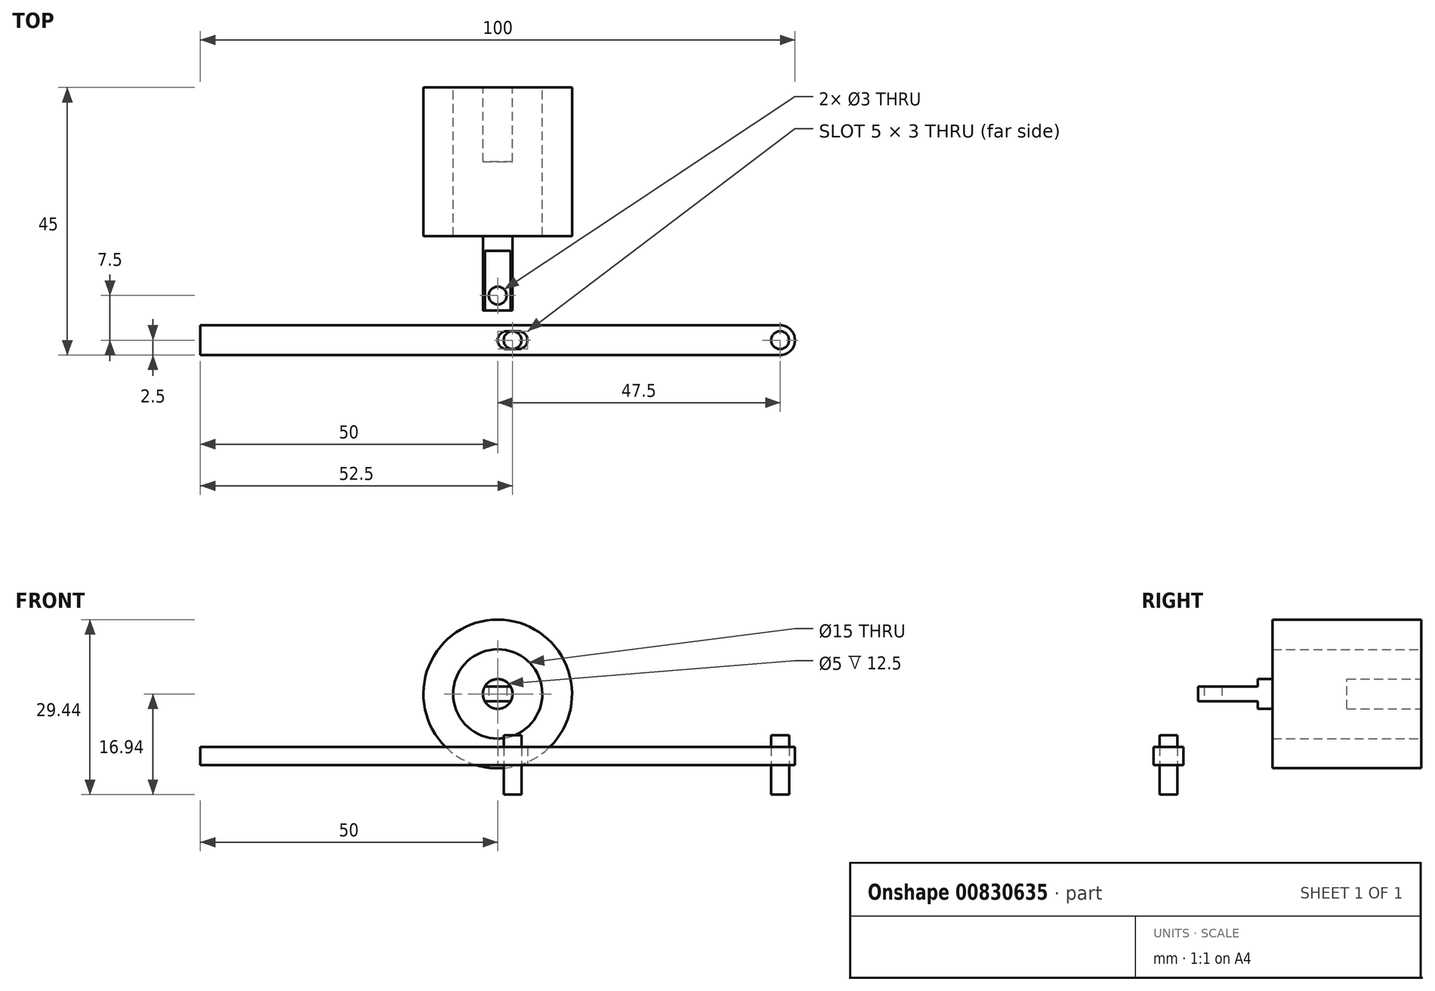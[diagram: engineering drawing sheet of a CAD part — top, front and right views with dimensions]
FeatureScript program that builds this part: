
annotation { "Feature Type Name" : "Feature", "Feature Type Description" : "" }
export const myFeature = defineFeature(function(context is Context, id is Id, definition is map)
    precondition{}
    {
        {
            var Q0;
            Q0=qCreatedBy(makeId("Top.planeOp"),FACE);
            var sketch = newSketch(context, id + "F0", { "sketchPlane" : qUnion([Q0])});
            skLineSegment(sketch, "E0.bottom", {"start": v(50, 2.5) * mm, "end": v(-50, 2.5) * mm});
            skLineSegment(sketch, "E0.top", {"start": v(50, -2.5) * mm, "end": v(-50, -2.5) * mm});
            skLineSegment(sketch, "E0.left", {"start": v(50, 2.5) * mm, "end": v(50, -2.5) * mm});
            skLineSegment(sketch, "E0.right", {"start": v(-50, 2.5) * mm, "end": v(-50, -2.5) * mm});
            skPoint(sketch, "E0.middle", {"position": v(0, 0) * mm});
            skCircle(sketch, "E1", {"center": v(47.5, 0) * mm, "radius": 1.5 * mm});
            skPoint(sketch, "E2.visualSharp", {"position": v(50, 2.5) * mm});
            skPoint(sketch, "E3.visualSharp", {"position": v(50, -2.5) * mm});
            skCircle(sketch, "E4", {"center": v(2.5, 0) * mm, "radius": 1.5 * mm});
            skLineSegment(sketch, "E5.bottom", {"start": v(5, -1.5) * mm, "end": v(0, -1.5) * mm});
            skLineSegment(sketch, "E5.top", {"start": v(5, 1.5) * mm, "end": v(0, 1.5) * mm});
            skLineSegment(sketch, "E5.left", {"start": v(5, -1.5) * mm, "end": v(5, 1.5) * mm});
            skLineSegment(sketch, "E5.right", {"start": v(0, -1.5) * mm, "end": v(0, 1.5) * mm});
            skCircle(sketch, "E6", {"center": v(1.5, 0) * mm, "radius": 1.5 * mm});
            skCircle(sketch, "E7", {"center": v(3.5, 0) * mm, "radius": 1.5 * mm});
            skCircle(sketch, "E8", {"center": v(47.5, 0) * mm, "radius": 2.5 * mm});
            skSolve(sketch);
        }
        {
            var Q0;
            {var subQ0=sQuery(id+"F0.wireOp",EDGE,"E5.right");var subQ1=sQuery(id+"F0.wireOp",EDGE,"E5.top");var subQ2=makeQuery(id+"F0.imprint","INTERSECT",VERTEX,{"derivedFrom":[subQ1,subQ0]});Q0=makeQuery(id+"F0.imprint","IMPRINT",FACE,{"disambiguationData":[TD([[makeQuery(id+"F0.imprint","IMPRINT",EDGE,{"disambiguationData":[TD([[subQ2,1.0]])],"derivedFrom":subQ1}),1.0]])]});}
            var Q1;
            {var subQ0=sQuery(id+"F0.wireOp",EDGE,"E5.right");var subQ1=sQuery(id+"F0.wireOp",EDGE,"E5.bottom");var subQ2=makeQuery(id+"F0.imprint","INTERSECT",VERTEX,{"derivedFrom":[subQ1,subQ0]});Q1=makeQuery(id+"F0.imprint","IMPRINT",FACE,{"disambiguationData":[TD([[makeQuery(id+"F0.imprint","IMPRINT",EDGE,{"disambiguationData":[TD([[subQ2,1.0]])],"derivedFrom":subQ1}),-1.0]])]});}
            var Q2;
            {var subQ0=sQuery(id+"F0.wireOp",EDGE,"E5.left");var subQ1=sQuery(id+"F0.wireOp",EDGE,"E5.bottom");var subQ2=makeQuery(id+"F0.imprint","INTERSECT",VERTEX,{"derivedFrom":[subQ1,subQ0]});Q2=makeQuery(id+"F0.imprint","IMPRINT",FACE,{"disambiguationData":[TD([[makeQuery(id+"F0.imprint","IMPRINT",EDGE,{"disambiguationData":[TD([[subQ2,-1.0]])],"derivedFrom":subQ1}),-1.0]])]});}
            var Q3;
            {var subQ0=sQuery(id+"F0.wireOp",EDGE,"E5.left");var subQ1=sQuery(id+"F0.wireOp",EDGE,"E5.top");var subQ2=makeQuery(id+"F0.imprint","INTERSECT",VERTEX,{"derivedFrom":[subQ1,subQ0]});Q3=makeQuery(id+"F0.imprint","IMPRINT",FACE,{"disambiguationData":[TD([[makeQuery(id+"F0.imprint","IMPRINT",EDGE,{"disambiguationData":[TD([[subQ2,-1.0]])],"derivedFrom":subQ1}),1.0]])]});}
            var Q4;
            {var subQ13=sQuery(id+"F0.wireOp",EDGE,"E0.right");Q4=makeQuery(id+"F0.imprint","IMPRINT",FACE,{"disambiguationData":[TD([[makeQuery(id+"F0.imprint","IMPRINT",EDGE,{"derivedFrom":subQ13}),1.0]])]});}
            var Q5;
            Q5=makeQuery(id+"F0.imprint","IMPRINT",FACE,{"disambiguationData":[TD([[makeQuery(id+"F0.imprint","IMPRINT",EDGE,{"derivedFrom":sQuery(id+"F0.wireOp",EDGE,"E1")}),-1.0]])]});
            extrude(context, id + "F1", {"entities" : qUnion([Q0, Q1, Q2, Q3, Q4, Q5]), "depth" : 3 * mm, "offsetDistance" : 25 * mm});
        }
        {
            var Q0;
            Q0=makeQuery(id+"F0.imprint","IMPRINT",FACE,{"disambiguationData":[TD([[makeQuery(id+"F0.imprint","IMPRINT",EDGE,{"derivedFrom":sQuery(id+"F0.wireOp",EDGE,"E4")}),1.0]])]});
            var Q1;
            Q1=makeQuery(id+"F0.imprint","IMPRINT",FACE,{"disambiguationData":[TD([[makeQuery(id+"F0.imprint","IMPRINT",EDGE,{"derivedFrom":sQuery(id+"F0.wireOp",EDGE,"E1")}),1.0]])]});
            var Q2;
            {var subQ0=sQuery(id+"F0.wireOp",EDGE,"E6");var subQ1=sQuery(id+"F0.wireOp",EDGE,"E4");var subQ2=makeQuery(id+"F0.imprint","INTERSECT",VERTEX,{"disambiguationData":[OD(0.0)],"derivedFrom":[subQ1,subQ0]});Q2=makeQuery(id+"F0.imprint","IMPRINT",FACE,{"disambiguationData":[TD([[makeQuery(id+"F0.imprint","IMPRINT",EDGE,{"disambiguationData":[TD([[subQ2,-1.0]])],"derivedFrom":subQ1}),1.0]])]});}
            var Q3;
            {var subQ0=sQuery(id+"F0.wireOp",EDGE,"E7");var subQ1=sQuery(id+"F0.wireOp",EDGE,"E4");var subQ2=makeQuery(id+"F0.imprint","INTERSECT",VERTEX,{"disambiguationData":[OD(0.0)],"derivedFrom":[subQ1,subQ0]});Q3=makeQuery(id+"F0.imprint","IMPRINT",FACE,{"disambiguationData":[TD([[makeQuery(id+"F0.imprint","IMPRINT",EDGE,{"disambiguationData":[TD([[subQ2,1.0]])],"derivedFrom":subQ1}),1.0]])]});}
            var Q4;
            {var subQ0=sQuery(id+"F0.wireOp",EDGE,"E7");var subQ1=sQuery(id+"F0.wireOp",EDGE,"E6");var subQ2=makeQuery(id+"F0.imprint","INTERSECT",VERTEX,{"disambiguationData":[OD(0.0)],"derivedFrom":[subQ1,subQ0]});Q4=makeQuery(id+"F0.imprint","IMPRINT",FACE,{"disambiguationData":[TD([[makeQuery(id+"F0.imprint","IMPRINT",EDGE,{"disambiguationData":[TD([[subQ2,1.0]])],"derivedFrom":subQ1}),1.0]])]});}
            extrude(context, id + "F2", {"entities" : qUnion([Q0, Q1, Q2, Q3, Q4]), "endBound" : BoundingType.SYMMETRIC, "depth" : 10 * mm, "offsetDistance" : 25 * mm});
        }
        {
            var Q0;
            Q0=qCreatedBy(makeId("Front.planeOp"),FACE);
            cPlane(context, id + "F3", {"entities" : qUnion([Q0]), "cplaneType" : CPlaneType.OFFSET, "offset" : 30 * mm, "oppositeDirection" : true, "width" : 150 * mm, "height" : 150 * mm});
        }
        {
            var Q0;
            Q0=qCreatedBy(id+"F3.planeOp",FACE);
            var sketch = newSketch(context, id + "F4", { "sketchPlane" : qUnion([Q0])});
            skCircle(sketch, "E9", {"center": v(0, 11.94) * mm, "radius": 12.5 * mm});
            skCircle(sketch, "E10", {"center": v(0, 11.94) * mm, "radius": 7.5 * mm});
            skCircle(sketch, "E11", {"center": v(0, 11.94) * mm, "radius": 2.5 * mm});
            skSolve(sketch);
        }
        {
            var Q0;
            Q0=makeQuery(id+"F4.imprint","IMPRINT",FACE,{"disambiguationData":[TD([[makeQuery(id+"F4.imprint","IMPRINT",EDGE,{"derivedFrom":sQuery(id+"F4.wireOp",EDGE,"E9")}),1.0]])]});
            extrude(context, id + "F5", {"entities" : qUnion([Q0]), "endBound" : BoundingType.SYMMETRIC, "depth" : 25 * mm, "offsetDistance" : 25 * mm});
        }
        {
            var Q0;
            Q0=makeQuery(id+"F4.imprint","IMPRINT",FACE,{"disambiguationData":[TD([[makeQuery(id+"F4.imprint","IMPRINT",EDGE,{"derivedFrom":sQuery(id+"F4.wireOp",EDGE,"E10")}),1.0]])]});
            extrude(context, id + "F6", {"entities" : qUnion([Q0]), "endBound" : BoundingType.SYMMETRIC, "depth" : 25 * mm, "offsetDistance" : 25 * mm});
        }
        {
            var Q0;
            Q0=makeQuery(id+"F4.imprint","IMPRINT",FACE,{"disambiguationData":[TD([[makeQuery(id+"F4.imprint","IMPRINT",EDGE,{"derivedFrom":sQuery(id+"F4.wireOp",EDGE,"E11")}),1.0]])]});
            extrude(context, id + "F7", {"entities" : qUnion([Q0]), "operationType" : NewBodyOperationType.ADD, "depth" : 25 * mm, "offsetDistance" : 25 * mm});
        }
        {
            var Q0;
            Q0=makeQuery(id+"F7.opExtrude","CAP_FACE",FACE,{"disambiguationData":[OSD([sQuery(id+"F4.wireOp",EDGE,"E11")])],"isStart":false});
            var sketch = newSketch(context, id + "F8", { "sketchPlane" : qUnion([Q0])});
            skLineSegment(sketch, "E12.bottom", {"start": v(3.5, 8.44) * mm, "end": v(-3.5, 8.44) * mm});
            skLineSegment(sketch, "E12.top", {"start": v(3.5, 15.44) * mm, "end": v(-3.5, 15.44) * mm});
            skLineSegment(sketch, "E12.left", {"start": v(3.5, 8.44) * mm, "end": v(3.5, 15.44) * mm});
            skLineSegment(sketch, "E12.right", {"start": v(-3.5, 8.44) * mm, "end": v(-3.5, 15.44) * mm});
            skPoint(sketch, "E12.middle", {"position": v(0, 11.94) * mm});
            skLineSegment(sketch, "E13.bottom", {"start": v(3.5, 13.19) * mm, "end": v(-3.5, 13.19) * mm});
            skLineSegment(sketch, "E13.top", {"start": v(3.5, 10.69) * mm, "end": v(-3.5, 10.69) * mm});
            skLineSegment(sketch, "E13.left", {"start": v(3.5, 13.19) * mm, "end": v(3.5, 10.69) * mm});
            skLineSegment(sketch, "E13.right", {"start": v(-3.5, 13.19) * mm, "end": v(-3.5, 10.69) * mm});
            skSolve(sketch);
        }
        {
            var Q0;
            {var subQ0=sQuery(id+"F8.wireOp",EDGE,"Uzw0eZBX-GlzA-F4h8-tydv-80rBA1psysMD");var subQ1=makeQuery(id+"F7.opExtrude","CAP_EDGE",EDGE,{"disambiguationData":[OSD([sQuery(id+"F4.wireOp",EDGE,"E11")])],"isStart":false});var subQ2=makeQuery(id+"F8.imprint","INTERSECT",VERTEX,{"disambiguationData":[OD(0.0)],"derivedFrom":[subQ1,subQ0]});Q0=makeQuery(id+"F8.imprint","IMPRINT",FACE,{"disambiguationData":[TD([[makeQuery(id+"F8.imprint","IMPRINT",EDGE,{"disambiguationData":[TD([[subQ2,-1.0]])],"derivedFrom":subQ0}),-1.0]])]});}
            var Q1;
            {var subQ0=sQuery(id+"F8.wireOp",EDGE,"E13.top");var subQ1=makeQuery(id+"F7.opExtrude","CAP_EDGE",EDGE,{"disambiguationData":[OSD([sQuery(id+"F4.wireOp",EDGE,"E11")])],"isStart":false});var subQ2=makeQuery(id+"F8.imprint","INTERSECT",VERTEX,{"disambiguationData":[OD(0.0)],"derivedFrom":[subQ1,subQ0]});Q1=makeQuery(id+"F8.imprint","IMPRINT",FACE,{"disambiguationData":[TD([[makeQuery(id+"F8.imprint","IMPRINT",EDGE,{"disambiguationData":[TD([[subQ2,-1.0]])],"derivedFrom":subQ0}),1.0]])]});}
            var Q2;
            {var subQ0=sQuery(id+"F8.wireOp",EDGE,"E13.bottom");var subQ1=makeQuery(id+"F7.opExtrude","CAP_EDGE",EDGE,{"disambiguationData":[OSD([sQuery(id+"F4.wireOp",EDGE,"E11")])],"isStart":false});var subQ2=makeQuery(id+"F8.imprint","INTERSECT",VERTEX,{"disambiguationData":[OD(0.0)],"derivedFrom":[subQ1,subQ0]});Q2=makeQuery(id+"F8.imprint","IMPRINT",FACE,{"disambiguationData":[TD([[makeQuery(id+"F8.imprint","IMPRINT",EDGE,{"disambiguationData":[TD([[subQ2,-1.0]])],"derivedFrom":subQ0}),-1.0]])]});}
            extrude(context, id + "F9", {"entities" : qUnion([Q0, Q1, Q2]), "operationType" : NewBodyOperationType.REMOVE, "oppositeDirection" : true, "depth" : 10 * mm, "offsetDistance" : 25 * mm});
        }
        {
            var Q0;
            Q0=makeQuery(id+"F9.boolean.opBoolean","COPY",FACE,{"derivedFrom":makeQuery(id+"F9.opExtrude","SWEPT_FACE",FACE,{"disambiguationData":[OSD([sQuery(id+"F8.wireOp",EDGE,"E13.top")])]})});
            var sketch = newSketch(context, id + "F10", { "sketchPlane" : qUnion([Q0])});
            skCircle(sketch, "E14", {"center": v(0, -7.5) * mm, "radius": 1.5 * mm});
            skPoint(sketch, "E14.centerSnap0", {"position": v(0, -5) * mm});
            skSolve(sketch);
        }
        {
            var Q0;
            Q0=makeQuery(id+"F10.imprint","IMPRINT",FACE,{"disambiguationData":[TD([[makeQuery(id+"F10.imprint","IMPRINT",EDGE,{"derivedFrom":sQuery(id+"F10.wireOp",EDGE,"E14")}),1.0]])]});
            extrude(context, id + "F11", {"entities" : qUnion([Q0]), "operationType" : NewBodyOperationType.REMOVE, "oppositeDirection" : true, "depth" : 25 * mm, "offsetDistance" : 25 * mm});
        }
    });
